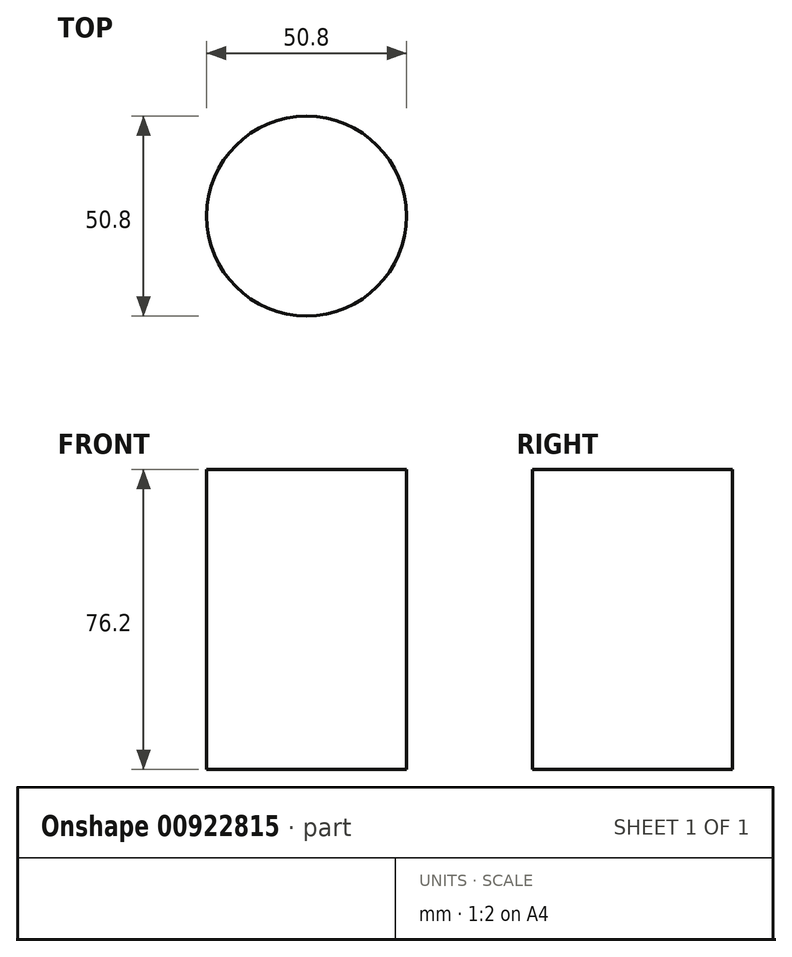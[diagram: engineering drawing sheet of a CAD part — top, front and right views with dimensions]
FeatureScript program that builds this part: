
annotation { "Feature Type Name" : "Feature", "Feature Type Description" : "" }
export const myFeature = defineFeature(function(context is Context, id is Id, definition is map)
    precondition{}
    {
        {
            var Q0;
            Q0=qCreatedBy(makeId("Top.planeOp"),FACE);
            var sketch = newSketch(context, id + "F0", { "sketchPlane" : qUnion([Q0])});
            skCircle(sketch, "E0", {"center": v(0, 0) * mm, "radius": 25.4 * mm});
            skSolve(sketch);
        }
        {
            var Q0;
            Q0=makeQuery(id+"F0.imprint","IMPRINT",FACE,{"disambiguationData":[TD([[makeQuery(id+"F0.imprint","IMPRINT",EDGE,{"derivedFrom":sQuery(id+"F0.wireOp",EDGE,"E0")}),1.0]])]});
            extrude(context, id + "F1", {"entities" : qUnion([Q0]), "depth" : 76.2 * mm, "offsetDistance" : 25.4 * mm});
        }
    });
